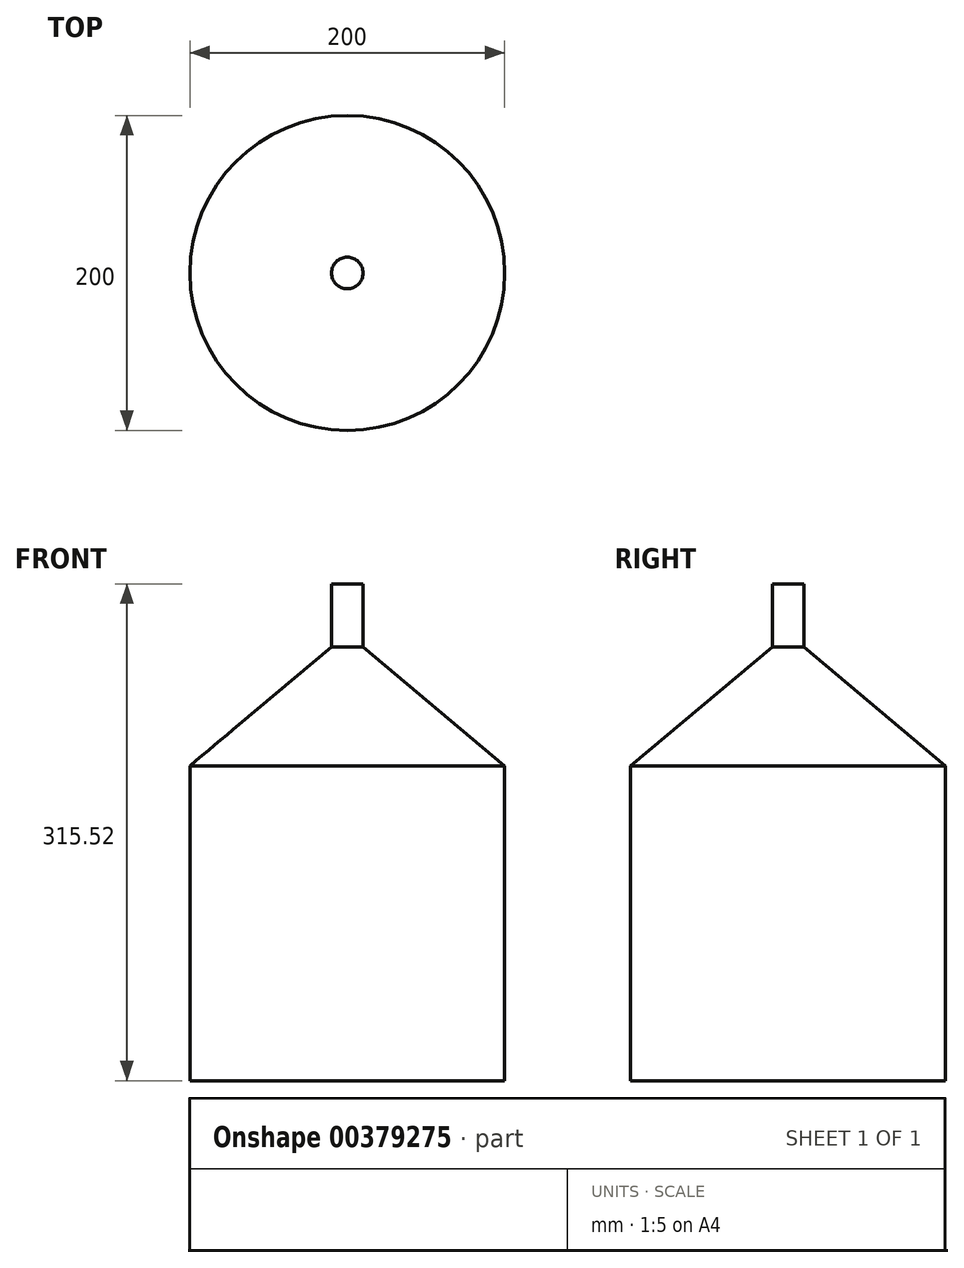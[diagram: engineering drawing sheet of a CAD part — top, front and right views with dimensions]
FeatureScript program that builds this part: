
annotation { "Feature Type Name" : "Feature", "Feature Type Description" : "" }
export const myFeature = defineFeature(function(context is Context, id is Id, definition is map)
    precondition{}
    {
        {
            var Q0;
            Q0=qCreatedBy(makeId("Front.planeOp"),FACE);
            var sketch = newSketch(context, id + "F0", { "sketchPlane" : qUnion([Q0])});
            skLineSegment(sketch, "E0", {"start": v(0, 315.52) * mm, "end": v(-10, 315.52) * mm});
            skLineSegment(sketch, "E1", {"start": v(-10, 315.52) * mm, "end": v(-10, 275.52) * mm});
            skLineSegment(sketch, "E2", {"start": v(-10, 275.52) * mm, "end": v(-100, 200) * mm});
            skLineSegment(sketch, "E3", {"start": v(-100, 200) * mm, "end": v(-100, 0) * mm});
            skLineSegment(sketch, "E4", {"start": v(-100, 0) * mm, "end": v(0, 0) * mm});
            skLineSegment(sketch, "E5", {"start": v(0, 0) * mm, "end": v(0, 315.52) * mm});
            skSolve(sketch);
        }
        {
            var Q0;
            Q0=makeQuery(id+"F0.imprint","IMPRINT",FACE,{"disambiguationData":[TD([[makeQuery(id+"F0.imprint","IMPRINT",EDGE,{"derivedFrom":sQuery(id+"F0.wireOp",EDGE,"E0")}),1.0]])]});
            var Q1;
            Q1=sQuery(id+"F0.wireOp",EDGE,"E5");
            revolve(context, id + "F1", {"entities" : qUnion([Q0]), "axis" : qUnion([Q1]), "revolveType" : RevolveType.FULL});
        }
    });
